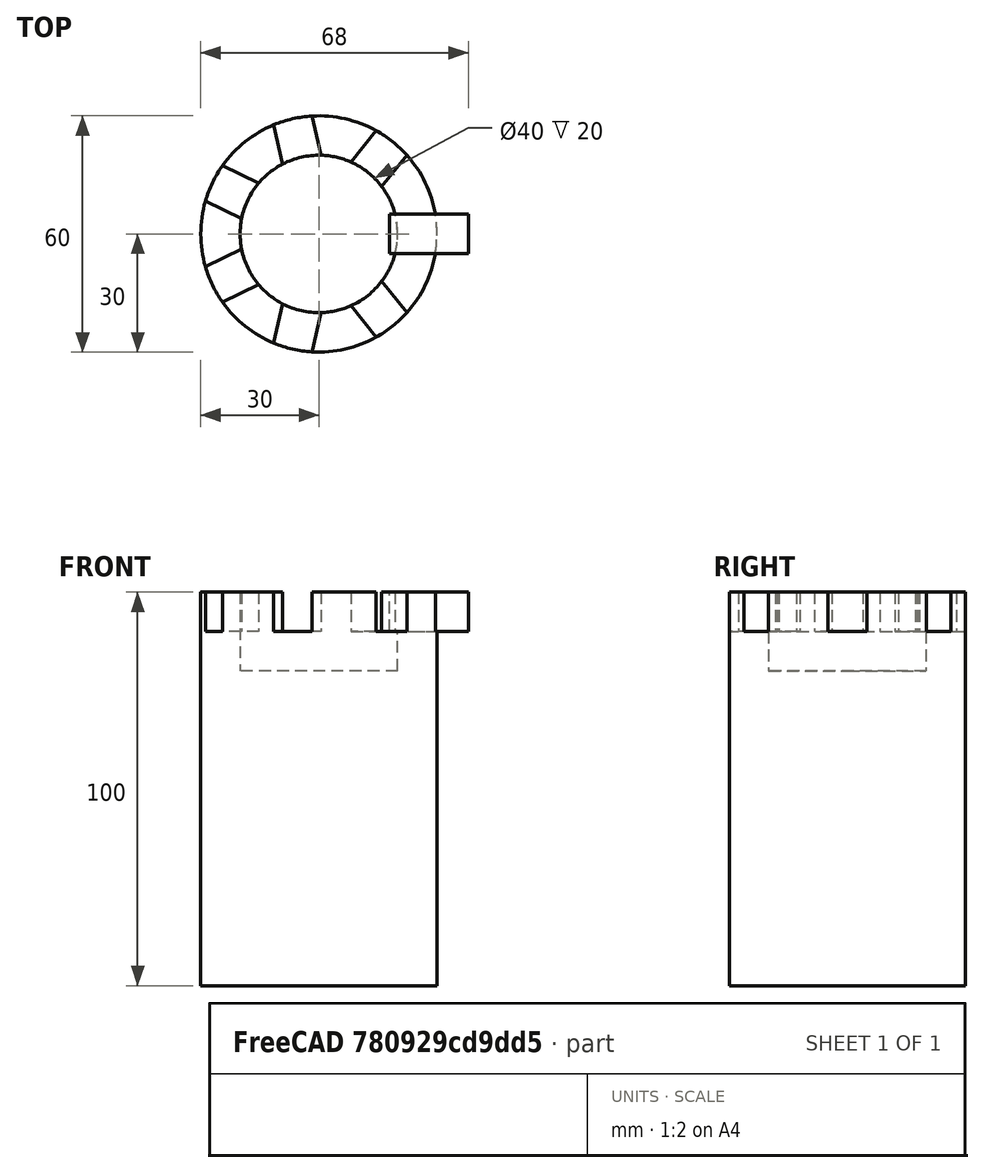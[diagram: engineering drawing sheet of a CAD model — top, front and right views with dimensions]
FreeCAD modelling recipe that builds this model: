
FCSTD DOCUMENT  (FreeCAD 1.0R39319 (Git))
Label: ojt1_t11r03_tower
License: All rights reserved
LicenseURL: https://en.wikipedia.org/wiki/All_rights_reserved
objects: Part::Cylinder×2, Part::Cut×2, Part::Box×1, Part::FeaturePython×1
note: 5 computed .brp shape members not serialized (recipe doc carries the construction recipe); baked Part::Feature solids carry a one-line shape summary decoded from their .brp

FEATURE [Part::Cylinder] Cylinder
  Angle = 360
  AttacherType = Attacher::AttachEngine3D
  FirstAngle = 0
  Height = 100
  Radius = 30
  SecondAngle = 0
FEATURE [Part::Cylinder] Cylinder001
  Angle = 360
  AttacherType = Attacher::AttachEngine3D
  FirstAngle = 0
  Height = 20
  Placement = pos=(0,0,80) rot=(0,0,1;0rad)
  Radius = 20
  SecondAngle = 0
FEATURE [Part::Cut] Cut
  Base = -> Cylinder
  Refine = true
  Tool = -> Cylinder001
FEATURE [Part::Box] Box  label="Cube"
  AttacherType = Attacher::AttachEngine3D
  Height = 10
  Length = 20
  Placement = pos=(18,-5,90) rot=(0,0,1;0rad)
  Width = 10
FEATURE [Part::FeaturePython] Array  # Draft array (typed FeaturePython)
  AlwaysSyncPlacement = false
  Angle = 360
  ArrayType = 1
  Axis = (0,0,1)
  Base = -> Box
  Center = (0,0,0)
  Count = 7
  ExpandArray = false
  Fuse = false
  IntervalAxis = (0,0,0)
  IntervalX = (50,0,0)
  IntervalY = (0,50,0)
  IntervalZ = (0,0,50)
  NumberCircles = 3
  NumberPolar = 7
  NumberX = 2
  NumberY = 2
  NumberZ = 1
  PlacementList = 7 placements: [(18,-5,90),(15.132,10.9555,90),(0.869263,18.6613,90),(-14.048,12.3148,90),(-18.3869,-3.30506,90),(-8.88002,-16.4361,90),(7.31366,-17.1904,90)]
  RadialDistance = 50
  ScaleList = (7) [(1,1,1),(1,1,1),(1,1,1),(1,1,1),(1,1,1),(1,1,1),(1,1,1)]
  Symmetry = 1
  TangentialDistance = 25
FEATURE [Part::Cut] Cut001
  Base = -> Cut
  Refine = true
  Tool = -> Array
